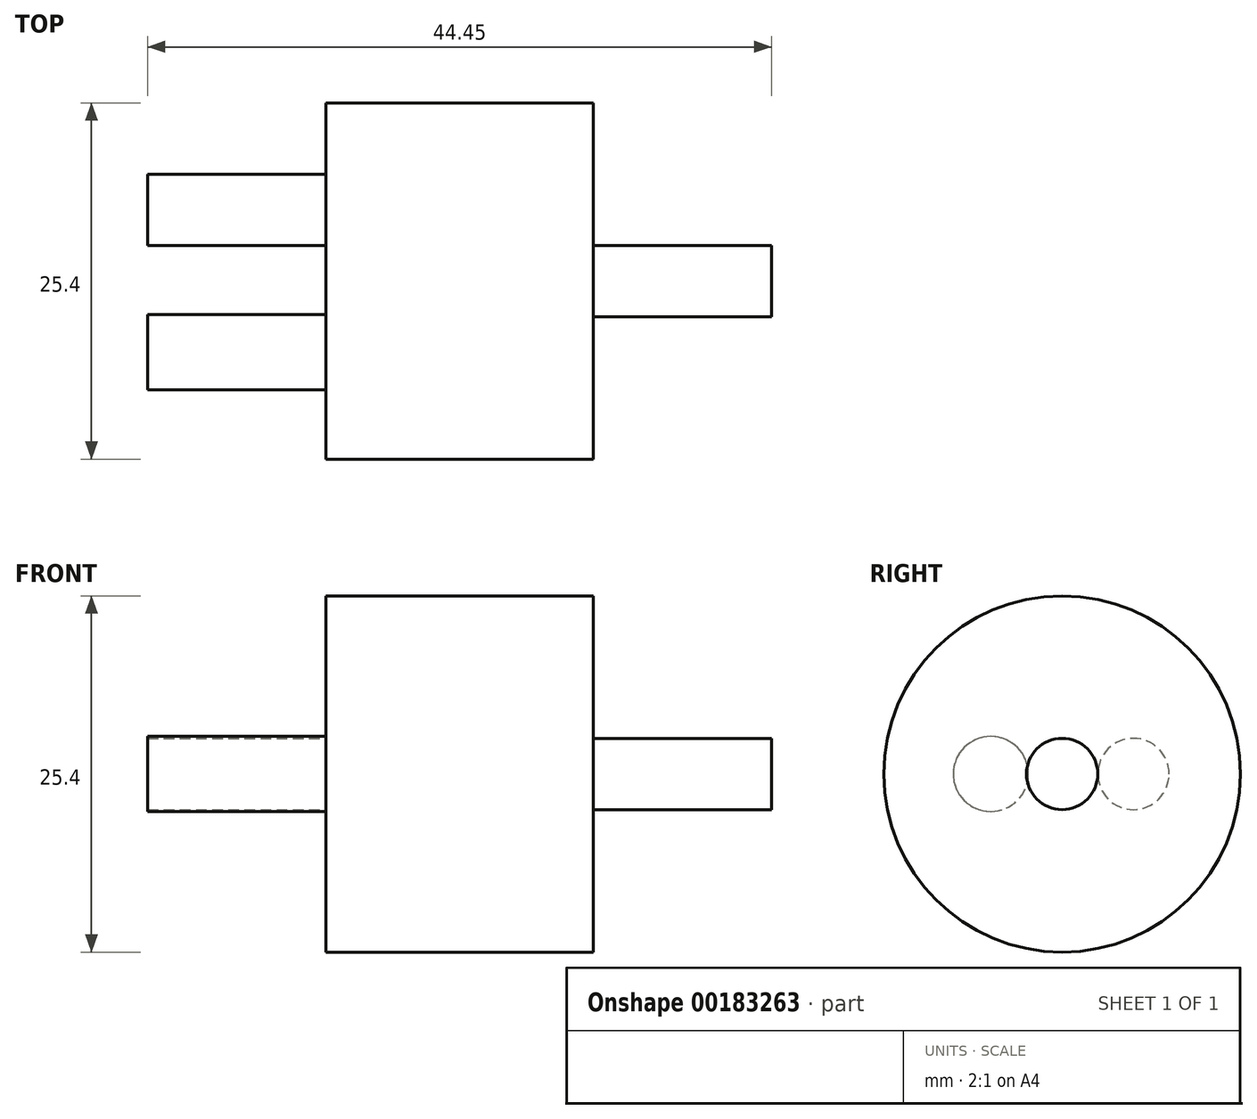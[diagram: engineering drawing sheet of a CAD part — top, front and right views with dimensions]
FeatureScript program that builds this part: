
annotation { "Feature Type Name" : "Feature", "Feature Type Description" : "" }
export const myFeature = defineFeature(function(context is Context, id is Id, definition is map)
    precondition{}
    {
        {
            var Q0;
            Q0=qCreatedBy(makeId("Right.planeOp"),FACE);
            var sketch = newSketch(context, id + "F0", { "sketchPlane" : qUnion([Q0])});
            skCircle(sketch, "E0", {"center": v(0, 0) * mm, "radius": 12.7 * mm});
            skSolve(sketch);
        }
        {
            var Q0;
            Q0=makeQuery(id+"F0.imprint","IMPRINT",FACE,{"disambiguationData":[TD([[makeQuery(id+"F0.imprint","IMPRINT",EDGE,{"derivedFrom":sQuery(id+"F0.wireOp",EDGE,"E0")}),1.0]])]});
            extrude(context, id + "F1", {"entities" : qUnion([Q0]), "depth" : 19.05 * mm});
        }
        {
            var Q0;
            Q0=makeQuery(id+"F1.opExtrude","CAP_FACE",FACE,{"disambiguationData":[OSD([sQuery(id+"F0.wireOp",EDGE,"E0")])],"isStart":false});
            var sketch = newSketch(context, id + "F2", { "sketchPlane" : qUnion([Q0])});
            skCircle(sketch, "E1", {"center": v(0, 0) * mm, "radius": 2.54 * mm});
            skSolve(sketch);
        }
        {
            var Q0;
            Q0=makeQuery(id+"F2.imprint","IMPRINT",FACE,{"disambiguationData":[TD([[makeQuery(id+"F2.imprint","IMPRINT",EDGE,{"derivedFrom":sQuery(id+"F2.wireOp",EDGE,"E1")}),1.0]])]});
            extrude(context, id + "F3", {"entities" : qUnion([Q0]), "operationType" : NewBodyOperationType.ADD, "depth" : 12.7 * mm});
        }
        {
            var Q0;
            Q0=makeQuery(id+"F1.opExtrude","CAP_FACE",FACE,{"disambiguationData":[OSD([sQuery(id+"F0.wireOp",EDGE,"E0")])],"isStart":true});
            var sketch = newSketch(context, id + "F4", { "sketchPlane" : qUnion([Q0])});
            skCircle(sketch, "E2", {"center": v(-5.08, 0) * mm, "radius": 2.54 * mm});
            skCircle(sketch, "E3", {"center": v(5.08, 0) * mm, "radius": 2.67 * mm});
            skSolve(sketch);
        }
        {
            var Q0;
            Q0=makeQuery(id+"F4.imprint","IMPRINT",FACE,{"disambiguationData":[TD([[makeQuery(id+"F4.imprint","IMPRINT",EDGE,{"derivedFrom":sQuery(id+"F4.wireOp",EDGE,"E2")}),1.0]])]});
            var Q1;
            Q1=makeQuery(id+"F4.imprint","IMPRINT",FACE,{"disambiguationData":[TD([[makeQuery(id+"F4.imprint","IMPRINT",EDGE,{"derivedFrom":sQuery(id+"F4.wireOp",EDGE,"E3")}),1.0]])]});
            extrude(context, id + "F5", {"entities" : qUnion([Q0, Q1]), "operationType" : NewBodyOperationType.ADD, "depth" : 12.7 * mm});
        }
    });
